# Revit family: ADB Fourneaux Gaz L6002
name_source: partatom
category: Equipement spécialisé
units: mm (PartAtom-declared; Revit-internal decimal feet)

## family parameters
Basée sur le plan de construction = Non
Conserver l'orientation des annotations = Non
Cote de connecteur circulaire = Utiliser le diamètre
Couper avec des vides une fois chargée = Non
Numéro OmniClass = 23.40.40.14.17.11
Partagée = Non
Repère de localisation dans la pièce = Non
Titre OmniClass = Cookers, Ovens, Stoves
Toujours verticalement = Oui
Type d'élément = Normal

## types (1)
- 4 feux vifs 1 four - CG 641 P
    Commentaires du type = Gamme Ambassade - Fourneaux gaz
    Description = Fourneau 4 feux vifs - 1 four gaz
    Diamètre de Raccordement Gaz = 21 mm
    Elévation par défaut = 0 mm  [stored 0 ft]
    Fabricant = Société Industrielle de Lacanche
    Modèle = CG 641 P
    Pbase = 0 W
    Poids net à vide = 78.00 kg
    URL = https://www.ambassade-de-bourgogne.com

note: [stored X ft] marks values corroborated as IEEE doubles in the binary element streams (Revit-internal decimal feet)
